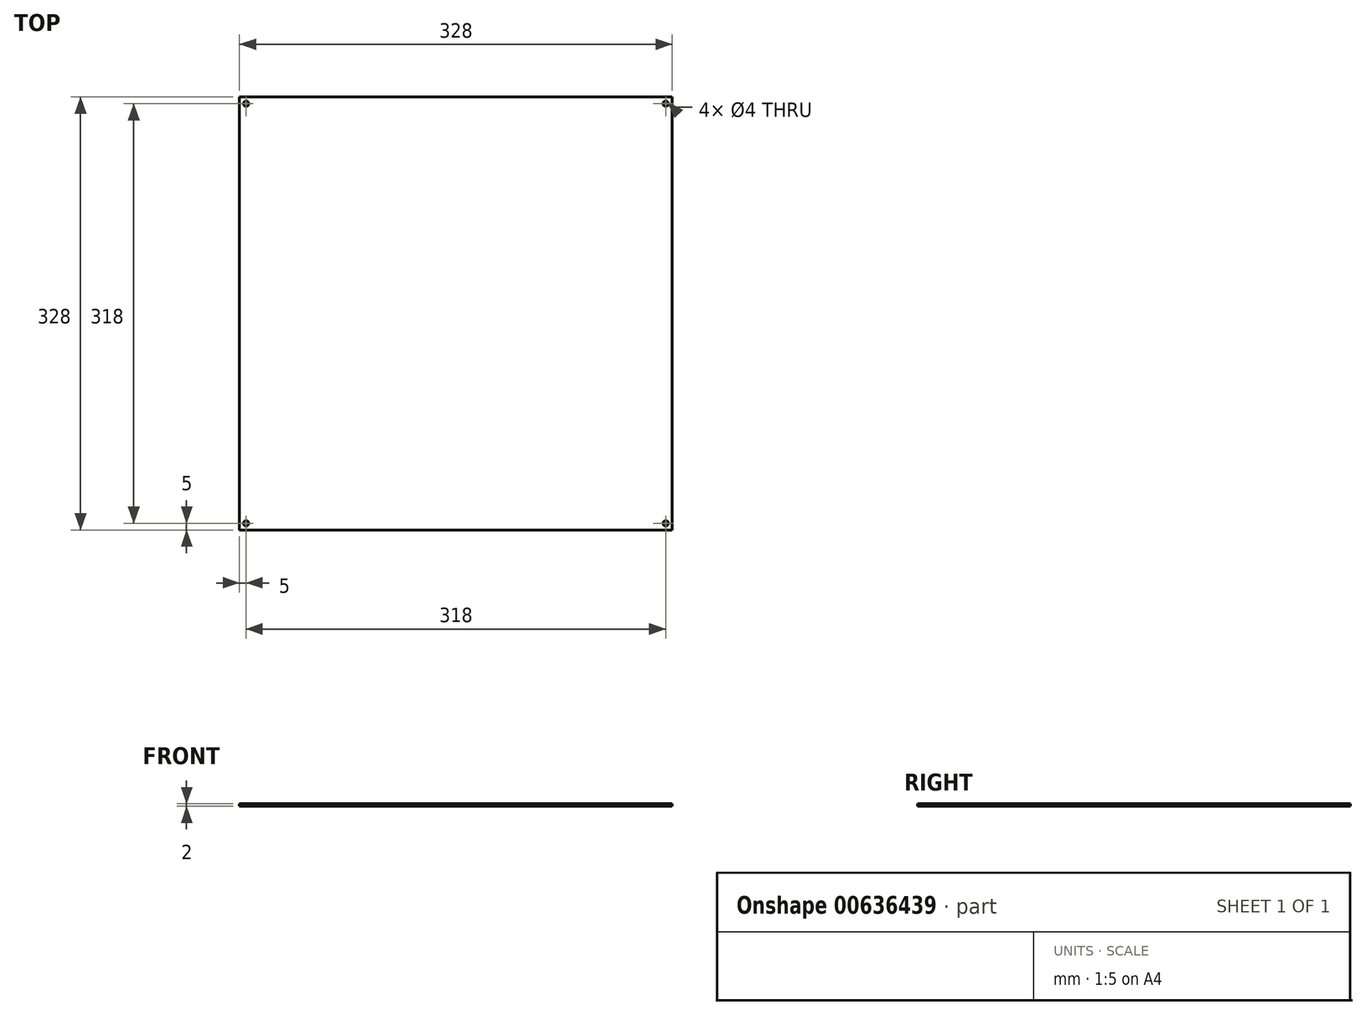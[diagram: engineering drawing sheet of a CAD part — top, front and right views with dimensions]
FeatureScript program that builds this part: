
annotation { "Feature Type Name" : "Feature", "Feature Type Description" : "" }
export const myFeature = defineFeature(function(context is Context, id is Id, definition is map)
    precondition{}
    {
        {
            var Q0;
            Q0=qCreatedBy(makeId("Top.planeOp"),FACE);
            var sketch = newSketch(context, id + "F0", { "sketchPlane" : qUnion([Q0])});
            skLineSegment(sketch, "E0.bottom", {"start": v(0, 0) * mm, "end": v(328, 0) * mm});
            skLineSegment(sketch, "E0.top", {"start": v(0, 328) * mm, "end": v(328, 328) * mm});
            skLineSegment(sketch, "E0.left", {"start": v(0, 0) * mm, "end": v(0, 328) * mm});
            skLineSegment(sketch, "E0.right", {"start": v(328, 0) * mm, "end": v(328, 328) * mm});
            skCircle(sketch, "E1", {"center": v(5, 5) * mm, "radius": 2 * mm});
            skLineSegment(sketch, "E2", {"start": v(164, 0) * mm, "end": v(164, 328) * mm, "construction": true});
            skLineSegment(sketch, "E3", {"start": v(0, 164) * mm, "end": v(328, 164) * mm, "construction": true});
            skCircle(sketch, "E4.MirrorC", {"center": v(323, 5) * mm, "radius": 2 * mm});
            skCircle(sketch, "E5.MirrorC", {"center": v(323, 323) * mm, "radius": 2 * mm});
            skCircle(sketch, "E6.MirrorC", {"center": v(5, 323) * mm, "radius": 2 * mm});
            skSolve(sketch);
        }
        {
            var Q0;
            Q0 = qSketchRegion(id + "F0", true);
            extrude(context, id + "F1", {"entities" : qUnion([Q0]), "depth" : 2 * mm, "offsetDistance" : 25 * mm});
        }
    });
